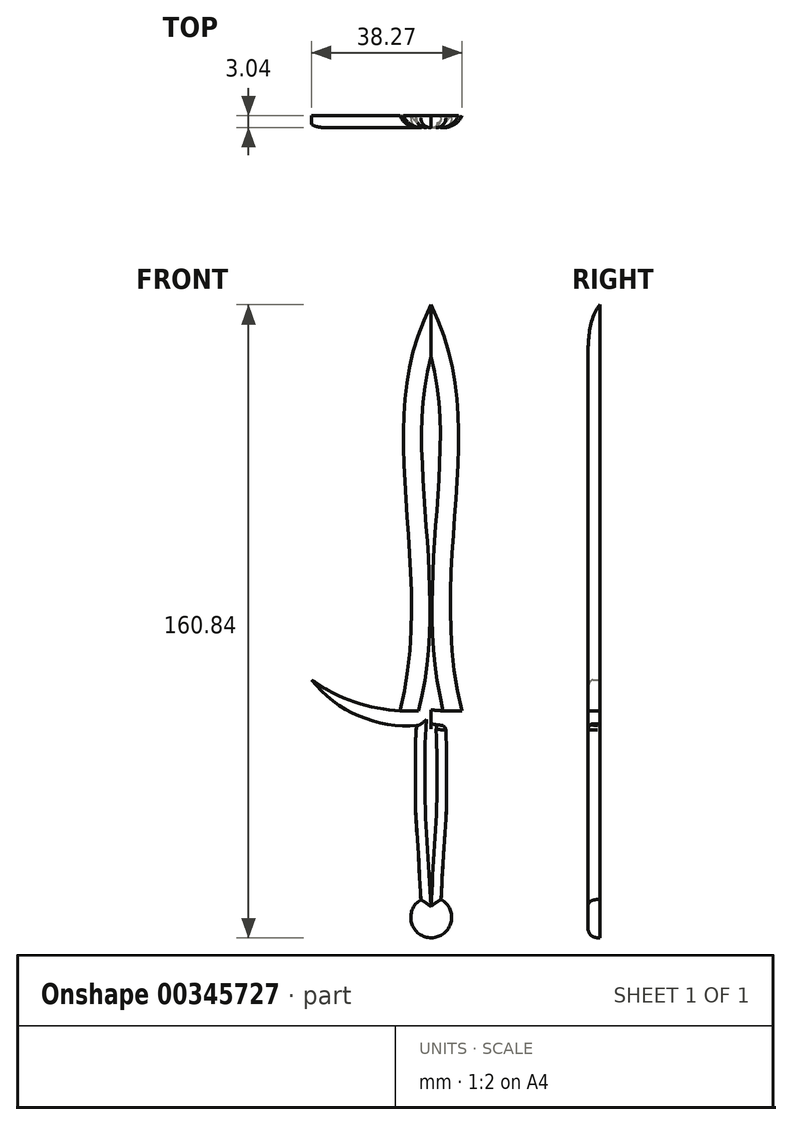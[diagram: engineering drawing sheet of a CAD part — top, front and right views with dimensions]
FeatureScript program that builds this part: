
annotation { "Feature Type Name" : "Feature", "Feature Type Description" : "" }
export const myFeature = defineFeature(function(context is Context, id is Id, definition is map)
    precondition{}
    {
        {
            var Q0;
            Q0=qCreatedBy(makeId("Front.planeOp"),FACE);
            var sketch = newSketch(context, id + "F0", { "sketchPlane" : qUnion([Q0])});
            skLineSegment(sketch, "E0", {"start": v(0, 75.74) * mm, "end": v(0, -74.71) * mm});
            skFitSpline(sketch, "E1", {"points": [v(0, 75.74) * mm, v(-6.9, 47.67) * mm, v(-5.56, 15.05) * mm, v(-7.9, -27.45) * mm], "startDerivative": vector(-45.44, -92.07) * mm, "endDerivative": vector(-30.62, -118.23) * mm});
            skFitSpline(sketch, "E2.MirrorCS", {"points": [v(0, 75.74) * mm, v(6.9, 47.67) * mm, v(5.56, 15.05) * mm, v(7.9, -27.45) * mm], "startDerivative": vector(45.44, -92.07) * mm, "endDerivative": vector(30.62, -118.23) * mm});
            skArc(sketch, "E3", {"start": v(-30.36, -19.54) * mm, "mid": v(-15.9, -26.24) * mm, "end": v(0, -27.15) * mm});
            skArc(sketch, "E4", {"start": v(-30.36, -19.54) * mm, "mid": v(-16.74, -29.36) * mm, "end": v(0, -30.72) * mm});
            skArc(sketch, "E5.MirrorCS", {"start": v(30.36, -19.54) * mm, "mid": v(16.74, -29.36) * mm, "end": v(0, -30.72) * mm});
            skArc(sketch, "E6.MirrorCS", {"start": v(30.36, -19.54) * mm, "mid": v(15.9, -26.24) * mm, "end": v(0, -27.15) * mm});
            skFitSpline(sketch, "E7", {"points": [v(-3.7, -31.2) * mm, v(-3.94, -42.14) * mm, v(-3.9, -52.44) * mm, v(-3.38, -61.18) * mm, v(-2.53, -76.5) * mm], "startDerivative": vector(-3.6, -44.46) * mm, "endDerivative": vector(2.02, -44.63) * mm});
            skFitSpline(sketch, "E8.MirrorCS", {"points": [v(3.7, -31.2) * mm, v(3.94, -42.14) * mm, v(3.9, -52.44) * mm, v(3.38, -61.18) * mm, v(2.53, -76.5) * mm], "startDerivative": vector(3.6, -44.46) * mm, "endDerivative": vector(-2.02, -44.63) * mm});
            skCircle(sketch, "E9", {"center": v(0.07, -79.9) * mm, "radius": 5.2 * mm});
            skPoint(sketch, "E9.second.point", {"position": v(0, -85.1) * mm});
            skPoint(sketch, "E9.third.point", {"position": v(-1.27, -84.92) * mm});
            skSolve(sketch);
        }
        {
            var Q0;
            {var subQ0=sQuery(id+"F0.wireOp",EDGE,"E2.MirrorCS");Q0=makeQuery(id+"F0.imprint","IMPRINT",FACE,{"disambiguationData":[TD([[makeQuery(id+"F0.imprint","IMPRINT",EDGE,{"derivedFrom":subQ0}),-1.0]])]});}
            var Q1;
            {var subQ1=sQuery(id+"F0.wireOp",EDGE,"E3");var subQ4=makeQuery(id+"F0.imprint","INTERSECT",VERTEX,{"derivedFrom":[sQuery(id+"F0.wireOp",EDGE,"E1"),subQ1]});Q1=makeQuery(id+"F0.imprint","IMPRINT",FACE,{"disambiguationData":[TD([[makeQuery(id+"F0.imprint","IMPRINT",EDGE,{"disambiguationData":[TD([[subQ4,1.0]])],"derivedFrom":subQ1}),-1.0]])]});}
            var Q2;
            {var subQ0=sQuery(id+"F0.wireOp",EDGE,"E5.MirrorCS");var subQ4=sQuery(id+"F0.wireOp",EDGE,"E6.MirrorCS");var subQ5=makeQuery(id+"F0.imprint","INTERSECT",VERTEX,{"derivedFrom":[subQ0,subQ4]});Q2=makeQuery(id+"F0.imprint","IMPRINT",FACE,{"disambiguationData":[TD([[makeQuery(id+"F0.imprint","IMPRINT",EDGE,{"disambiguationData":[TD([[subQ5,-1.0]])],"derivedFrom":subQ0}),-1.0]])]});}
            var Q3;
            {var subQ0=sQuery(id+"F0.wireOp",EDGE,"E1");Q3=makeQuery(id+"F0.imprint","IMPRINT",FACE,{"disambiguationData":[TD([[makeQuery(id+"F0.imprint","IMPRINT",EDGE,{"derivedFrom":subQ0}),1.0]])]});}
            var Q4;
            {var subQ3=sQuery(id+"F0.wireOp",EDGE,"E4");var subQ5=sQuery(id+"F0.wireOp",EDGE,"E7");var subQ6=makeQuery(id+"F0.imprint","INTERSECT",VERTEX,{"derivedFrom":[subQ3,subQ5]});Q4=makeQuery(id+"F0.imprint","IMPRINT",FACE,{"disambiguationData":[TD([[makeQuery(id+"F0.imprint","IMPRINT",EDGE,{"disambiguationData":[TD([[subQ6,-1.0]])],"derivedFrom":subQ5}),1.0]])]});}
            var Q5;
            {var subQ3=sQuery(id+"F0.wireOp",EDGE,"E5.MirrorCS");var subQ5=sQuery(id+"F0.wireOp",EDGE,"E8.MirrorCS");var subQ6=makeQuery(id+"F0.imprint","INTERSECT",VERTEX,{"derivedFrom":[subQ3,subQ5]});Q5=makeQuery(id+"F0.imprint","IMPRINT",FACE,{"disambiguationData":[TD([[makeQuery(id+"F0.imprint","IMPRINT",EDGE,{"disambiguationData":[TD([[subQ6,-1.0]])],"derivedFrom":subQ5}),-1.0]])]});}
            var Q6;
            {var subQ0=sQuery(id+"F0.wireOp",EDGE,"E9");var subQ1=makeQuery(id+"F0.imprint","INTERSECT",VERTEX,{"derivedFrom":[sQuery(id+"F0.wireOp",EDGE,"E0"),subQ0]});Q6=makeQuery(id+"F0.imprint","IMPRINT",FACE,{"disambiguationData":[TD([[makeQuery(id+"F0.imprint","IMPRINT",EDGE,{"disambiguationData":[TD([[subQ1,1.0]])],"derivedFrom":subQ0}),1.0]])]});}
            extrude(context, id + "F1", {"entities" : qUnion([Q0, Q1, Q2, Q3, Q4, Q5, Q6]), "endBound" : BoundingType.SYMMETRIC, "depth" : 3.05 * mm});
        }
        {
            var Q0;
            Q0=makeQuery(id+"F1.opExtrude","CAP_EDGE",EDGE,{"disambiguationData":[OSD([sQuery(id+"F0.wireOp",EDGE,"E1")])],"isStart":false});
            var Q1;
            Q1=makeQuery(id+"F1.opExtrude","CAP_EDGE",EDGE,{"disambiguationData":[OSD([sQuery(id+"F0.wireOp",EDGE,"E2.MirrorCS")])],"isStart":false});
            fillet(context, id + "F2", {"entities" : qUnion([Q0, Q1]), "radius" : 5.08 * mm, "tangentPropagation" : true, "allowEdgeOverflow" : false});
        }
        {
            var Q0;
            Q0=makeQuery(id+"F1.opExtrude","CAP_EDGE",EDGE,{"disambiguationData":[OSD([sQuery(id+"F0.wireOp",EDGE,"E7")])],"isStart":false});
            var Q1;
            Q1=makeQuery(id+"F1.opExtrude","CAP_EDGE",EDGE,{"disambiguationData":[OSD([sQuery(id+"F0.wireOp",EDGE,"E8.MirrorCS")])],"isStart":false});
            var Q2;
            Q2=makeQuery(id+"F1.opExtrude","CAP_EDGE",EDGE,{"disambiguationData":[OSD([sQuery(id+"F0.wireOp",EDGE,"E9")])],"isStart":false});
            fillet(context, id + "F3", {"entities" : qUnion([Q0, Q1, Q2]), "radius" : 2.45 * mm, "tangentPropagation" : true, "allowEdgeOverflow" : false});
        }
        {
            var Q0;
            Q0=makeQuery(id+"F1.opExtrude","CAP_EDGE",EDGE,{"disambiguationData":[OSD([sQuery(id+"F0.wireOp",EDGE,"E4")])],"isStart":false});
            var Q1;
            Q1=makeQuery(id+"F1.opExtrude","CAP_EDGE",EDGE,{"disambiguationData":[OSD([sQuery(id+"F0.wireOp",EDGE,"E5.MirrorCS")])],"isStart":false});
            fillet(context, id + "F4", {"entities" : qUnion([Q0, Q1]), "radius" : 1.23 * mm, "tangentPropagation" : true, "allowEdgeOverflow" : false});
        }
    });
